# Revit family: Haworth_Aloha_Active_Chair_Task_AP_PRELIMINARY
name_source: partatom
category: Furniture
units: mm (PartAtom-declared; Revit-internal decimal feet)

## family parameters
Always vertical = Yes
Cut with Voids When Loaded = No
OmniClass Number = 23.40.70.14.64.11
OmniClass Title = Office Furniture
Room Calculation Point = No
Shared = No
Work Plane-Based = No

## types (6) — shared parameters
Arm Finish = Haworth _ Paint _ Smoke
Assembly Code = E2020200
Caster Finish = Haworth _ Polymer _ Undecided
Depth = 737 mm
Description = Haworth - Aloha - Active - Task - Chair
Manufacturer = Haworth
Model = SECMTMX
Revision Number = 1
Size = Verify Final.Dim w/Haworth
URL = https://www.haworth.com
URL - Product = https://www.haworth.com
Warranty = http://www.haworth.com
Width = 737 mm

## per-type parameters (varying)
| type | 4D Arms | Height Adjustable Arms | With Arms | Without Arms |
| 4D Arms - Mesh Back | Yes | No | Yes | No |
| No Arms - Mesh Back | No | No | No | Yes |
| Height Adjustable Arms - Mesh Back | No | Yes | Yes | No |
| 4D Arms - Upholstered Back | Yes | No | Yes | No |
| Height Adjustable Arms - Upholstered Back | No | Yes | Yes | No |
| No Arms - Upholstered Back | No | No | No | Yes |

## geometry (parser evidence)
native form markers: Blend x2, Sweep x11
no freeform markers — native parametric forms only
